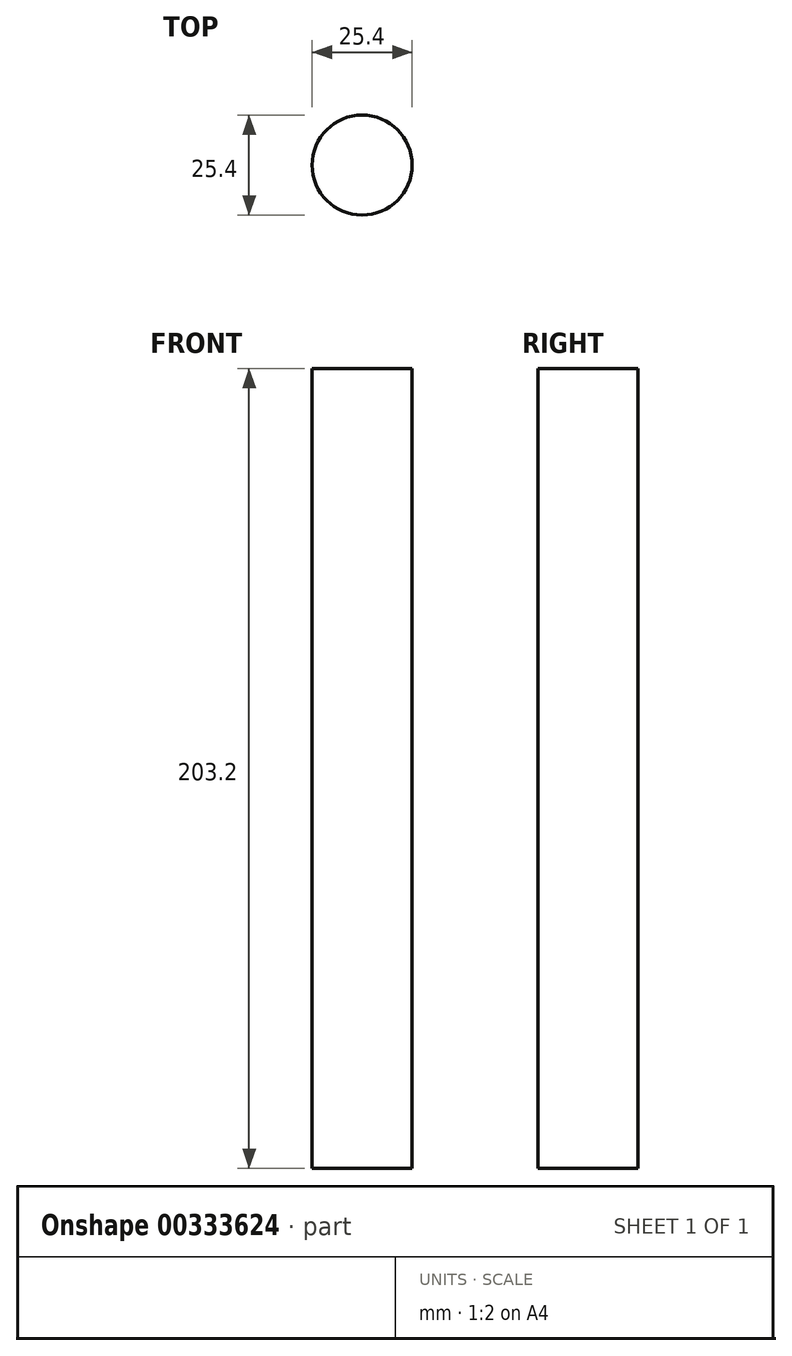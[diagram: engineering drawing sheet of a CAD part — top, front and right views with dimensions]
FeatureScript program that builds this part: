
annotation { "Feature Type Name" : "Feature", "Feature Type Description" : "" }
export const myFeature = defineFeature(function(context is Context, id is Id, definition is map)
    precondition{}
    {
        {
            var Q0;
            Q0=qCreatedBy(makeId("Top.planeOp"),FACE);
            var sketch = newSketch(context, id + "F0", { "sketchPlane" : qUnion([Q0])});
            skCircle(sketch, "E0", {"center": v(0, 0) * mm, "radius": 12.7 * mm});
            skSolve(sketch);
        }
        {
            var Q0;
            Q0=makeQuery(id+"F0.imprint","IMPRINT",FACE,{"disambiguationData":[TD([[makeQuery(id+"F0.imprint","IMPRINT",EDGE,{"derivedFrom":sQuery(id+"F0.wireOp",EDGE,"E0")}),1.0]])]});
            extrude(context, id + "F1", {"entities" : qUnion([Q0]), "depth" : 203.2 * mm});
        }
    });
